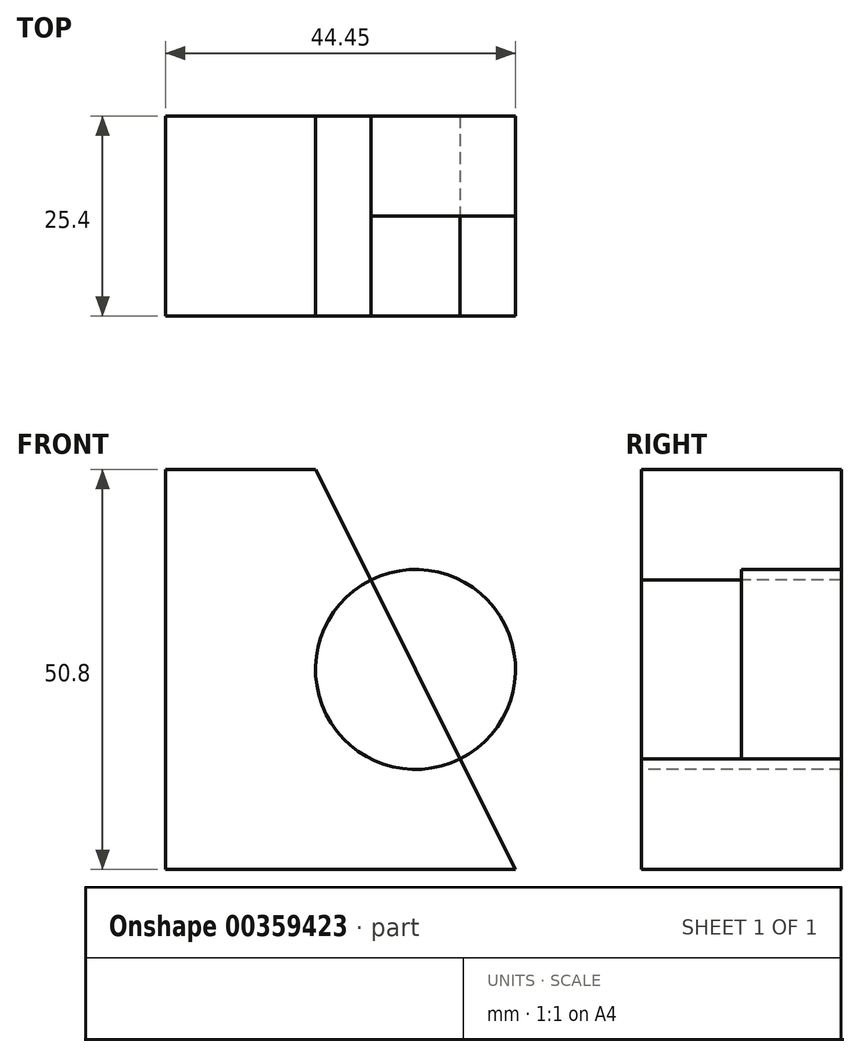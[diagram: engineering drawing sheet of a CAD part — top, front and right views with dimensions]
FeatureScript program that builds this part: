
annotation { "Feature Type Name" : "Feature", "Feature Type Description" : "" }
export const myFeature = defineFeature(function(context is Context, id is Id, definition is map)
    precondition{}
    {
        {
            var Q0;
            Q0=qCreatedBy(makeId("Front.planeOp"),FACE);
            var sketch = newSketch(context, id + "F0", { "sketchPlane" : qUnion([Q0])});
            skLineSegment(sketch, "E0", {"start": v(0, 0) * mm, "end": v(0, 50.8) * mm});
            skLineSegment(sketch, "E1", {"start": v(0, 50.8) * mm, "end": v(57.15, 50.8) * mm});
            skLineSegment(sketch, "E2", {"start": v(57.15, 50.8) * mm, "end": v(57.15, 0) * mm});
            skLineSegment(sketch, "E3", {"start": v(57.15, 0) * mm, "end": v(0, 0) * mm});
            skSolve(sketch);
        }
        {
            var Q0;
            Q0 = qSketchRegion(id + "F0", true);
            extrude(context, id + "F1", {"entities" : qUnion([Q0]), "depth" : 25.4 * mm});
        }
        {
            var Q0;
            Q0=makeQuery(id+"F1.opExtrude","CAP_FACE",FACE,{"disambiguationData":[OSD([sQuery(id+"F0.wireOp",EDGE,"E0"),sQuery(id+"F0.wireOp",EDGE,"E1"),sQuery(id+"F0.wireOp",EDGE,"E2"),sQuery(id+"F0.wireOp",EDGE,"E3")])],"isStart":false});
            var sketch = newSketch(context, id + "F2", { "sketchPlane" : qUnion([Q0])});
            skLineSegment(sketch, "E4", {"start": v(57.15, 0) * mm, "end": v(44.45, 0) * mm});
            skLineSegment(sketch, "E5", {"start": v(44.45, 0) * mm, "end": v(19.05, 50.8) * mm});
            skLineSegment(sketch, "E6", {"start": v(19.05, 50.8) * mm, "end": v(57.15, 50.8) * mm});
            skLineSegment(sketch, "E7", {"start": v(57.15, 50.8) * mm, "end": v(57.15, 0) * mm});
            skSolve(sketch);
        }
        {
            var Q0;
            Q0 = qSketchRegion(id + "F2", true);
            extrude(context, id + "F3", {"entities" : qUnion([Q0]), "operationType" : NewBodyOperationType.REMOVE, "oppositeDirection" : true, "depth" : 12.7 * mm});
        }
        {
            var Q0;
            Q0=makeQuery(id+"F1.opExtrude","CAP_FACE",FACE,{"disambiguationData":[OSD([sQuery(id+"F0.wireOp",EDGE,"E0"),sQuery(id+"F0.wireOp",EDGE,"E1"),sQuery(id+"F0.wireOp",EDGE,"E2"),sQuery(id+"F0.wireOp",EDGE,"E3")])],"isStart":false});
            var sketch = newSketch(context, id + "F4", { "sketchPlane" : qUnion([Q0])});
            skCircle(sketch, "E8", {"center": v(31.75, 25.4) * mm, "radius": 12.7 * mm});
            skSolve(sketch);
        }
        {
            var Q0;
            {var subQ0=sQuery(id+"F4.wireOp",EDGE,"E8");var subQ1=makeQuery(id+"F3.boolean.opBoolean","COPY",EDGE,{"derivedFrom":makeQuery(id+"F3.opExtrude","CAP_EDGE",EDGE,{"disambiguationData":[OSD([sQuery(id+"F2.wireOp",EDGE,"E5")])],"isStart":true})});var subQ2=makeQuery(id+"F4.imprint","INTERSECT",VERTEX,{"disambiguationData":[OD(0.0)],"derivedFrom":[subQ1,subQ0]});Q0=makeQuery(id+"F4.imprint","IMPRINT",FACE,{"disambiguationData":[TD([[makeQuery(id+"F4.imprint","IMPRINT",EDGE,{"disambiguationData":[TD([[subQ2,1.0]])],"derivedFrom":subQ0}),1.0]])]});}
            extrude(context, id + "F5", {"entities" : qUnion([Q0]), "operationType" : NewBodyOperationType.REMOVE, "oppositeDirection" : true, "depth" : 25.4 * mm});
        }
        {
            var Q0;
            Q0=makeQuery(id+"F3.boolean.opBoolean","COPY",FACE,{"derivedFrom":makeQuery(id+"F3.opExtrude","CAP_FACE",FACE,{"disambiguationData":[OSD([sQuery(id+"F2.wireOp",EDGE,"E4"),sQuery(id+"F2.wireOp",EDGE,"E5"),sQuery(id+"F2.wireOp",EDGE,"E6"),sQuery(id+"F2.wireOp",EDGE,"E7")])],"isStart":false})});
            var sketch = newSketch(context, id + "F6", { "sketchPlane" : qUnion([Q0])});
            skCircle(sketch, "E9", {"center": v(31.75, 25.4) * mm, "radius": 12.7 * mm});
            skSolve(sketch);
        }
        {
            var Q0;
            {var subQ1=sQuery(id+"F2.wireOp",EDGE,"E5");var subQ2=makeQuery(id+"F3.boolean.opBoolean","COPY",FACE,{"derivedFrom":makeQuery(id+"F3.opExtrude","CAP_FACE",FACE,{"disambiguationData":[OSD([sQuery(id+"F2.wireOp",EDGE,"E4"),subQ1,sQuery(id+"F2.wireOp",EDGE,"E6"),sQuery(id+"F2.wireOp",EDGE,"E7")])],"isStart":false})});var subQ3=makeQuery(id+"F5.opExtrude","SWEPT_FACE",FACE,{"disambiguationData":[OSD([subQ1])]});var subQ4=makeQuery(id+"F3.boolean.opBoolean","COPY",EDGE,{"derivedFrom":makeQuery(id+"F3.opExtrude","CAP_EDGE",EDGE,{"disambiguationData":[OSD([subQ1])],"isStart":false})});var subQ5=makeQuery(id+"F5.boolean.opBoolean","SPLIT",EDGE,{"disambiguationData":[topologyDisambiguationEdgeConnected([subQ2,subQ3])],"derivedFrom":subQ4});Q0=makeQuery(id+"F6.imprint","IMPRINT",FACE,{"disambiguationData":[TD([[makeQuery(id+"F6.imprint","IMPRINT",EDGE,{"derivedFrom":subQ5}),-1.0]])]});}
            extrude(context, id + "F7", {"entities" : qUnion([Q0]), "operationType" : NewBodyOperationType.REMOVE, "oppositeDirection" : true, "depth" : 25.4 * mm});
        }
    });
